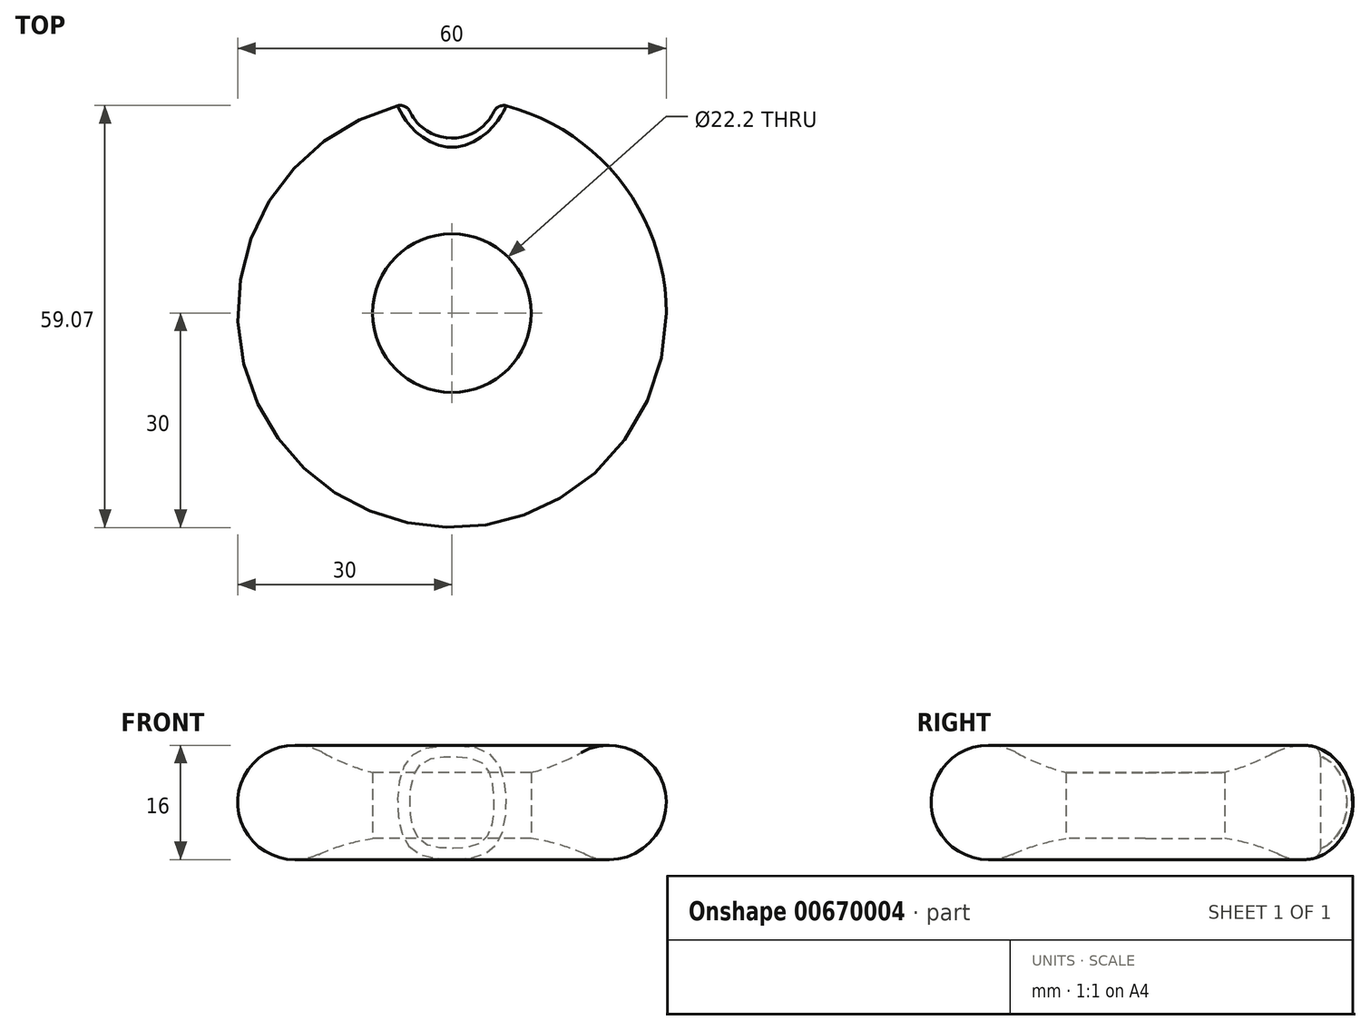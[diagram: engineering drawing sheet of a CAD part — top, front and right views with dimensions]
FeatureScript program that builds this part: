
annotation { "Feature Type Name" : "Feature", "Feature Type Description" : "" }
export const myFeature = defineFeature(function(context is Context, id is Id, definition is map)
    precondition{}
    {
        {
            var Q0;
            Q0=qCreatedBy(makeId("Right.planeOp"),FACE);
            var sketch = newSketch(context, id + "F0", { "sketchPlane" : qUnion([Q0])});
            skArc(sketch, "E0", {"start": v(-18.1, 14.99) * mm, "mid": v(-30, 8.33) * mm, "end": v(-18.7, 0.72) * mm});
            skPoint(sketch, "E1", {"position": v(-17.06, 7.86) * mm});
            skArc(sketch, "E2", {"start": v(0, 2.59) * mm, "mid": v(-9.5, 3.19) * mm, "end": v(-18.7, 0.72) * mm});
            skArc(sketch, "E3", {"start": v(-18.1, 14.99) * mm, "mid": v(-9.33, 11.8) * mm, "end": v(0, 11.53) * mm});
            skPoint(sketch, "E4.orphan", {"position": v(-16.89, 14.15) * mm});
            skPoint(sketch, "E5.orphan", {"position": v(-17.24, 1.57) * mm});
            skLineSegment(sketch, "E6", {"start": v(0, 11.53) * mm, "end": v(0, 2.59) * mm});
            skPoint(sketch, "E7.orphan", {"position": v(0, 13.3) * mm});
            skLineSegment(sketch, "E8.bottom", {"start": v(-3.38, 11.28) * mm, "end": v(1.79, 11.28) * mm});
            skLineSegment(sketch, "E8.top", {"start": v(-3.38, 13.04) * mm, "end": v(1.79, 13.04) * mm});
            skLineSegment(sketch, "E8.left", {"start": v(-3.38, 11.28) * mm, "end": v(-3.38, 13.04) * mm});
            skLineSegment(sketch, "E8.right", {"start": v(1.79, 11.28) * mm, "end": v(1.79, 13.04) * mm});
            skLineSegment(sketch, "E9.bottom", {"start": v(-5.05, 3.3) * mm, "end": v(5.31, 3.3) * mm});
            skLineSegment(sketch, "E9.top", {"start": v(-5.05, 0.65) * mm, "end": v(5.31, 0.65) * mm});
            skLineSegment(sketch, "E9.left", {"start": v(-5.05, 3.3) * mm, "end": v(-5.05, 0.65) * mm});
            skLineSegment(sketch, "E9.right", {"start": v(5.31, 3.3) * mm, "end": v(5.31, 0.65) * mm});
            skLineSegment(sketch, "E10.bottom", {"start": v(-5.05, 11.3) * mm, "end": v(3.19, 11.3) * mm});
            skLineSegment(sketch, "E10.top", {"start": v(-5.05, 12.11) * mm, "end": v(3.19, 12.11) * mm});
            skLineSegment(sketch, "E10.left", {"start": v(-5.05, 11.3) * mm, "end": v(-5.05, 12.11) * mm});
            skLineSegment(sketch, "E10.right", {"start": v(3.19, 11.3) * mm, "end": v(3.19, 12.11) * mm});
            skSolve(sketch);
        }
        {
            var Q0;
            {var subQ4=sQuery(id+"F0.wireOp",EDGE,"E0");Q0=makeQuery(id+"F0.imprint","IMPRINT",FACE,{"disambiguationData":[TD([[makeQuery(id+"F0.imprint","IMPRINT",EDGE,{"derivedFrom":subQ4}),1.0]])]});}
            var Q1;
            Q1=sQuery(id+"F0.wireOp",EDGE,"E6");
            revolve(context, id + "F1", {"entities" : qUnion([Q0]), "axis" : qUnion([Q1]), "revolveType" : RevolveType.FULL});
        }
        {
            var Q0;
            Q0=qCreatedBy(makeId("Top.planeOp"),FACE);
            var sketch = newSketch(context, id + "F2", { "sketchPlane" : qUnion([Q0])});
            skCircle(sketch, "E11", {"center": v(0, 0) * mm, "radius": 11.1 * mm});
            skSolve(sketch);
        }
        {
            var Q0;
            Q0 = qSketchRegion(id + "F2", true);
            extrude(context, id + "F3", {"entities" : qUnion([Q0]), "operationType" : NewBodyOperationType.REMOVE, "depth" : 25 * mm, "offsetDistance" : 25 * mm});
        }
        {
            var Q0;
            Q0=qCreatedBy(makeId("Top.planeOp"),FACE);
            var sketch = newSketch(context, id + "F4", { "sketchPlane" : qUnion([Q0])});
            skCircle(sketch, "E12", {"center": v(0, 31) * mm, "radius": 6.5 * mm});
            skSolve(sketch);
        }
        {
            var Q0;
            Q0 = qSketchRegion(id + "F4", true);
            extrude(context, id + "F5", {"entities" : qUnion([Q0]), "operationType" : NewBodyOperationType.REMOVE, "depth" : 25 * mm, "offsetDistance" : 25 * mm});
        }
        {
            var Q0;
            Q0=makeQuery(id+"F5.boolean.opBoolean","INTERSECT",EDGE,{"derivedFrom":[makeQuery(id+"F1.opRevolve","SWEPT_FACE",FACE,{"disambiguationData":[OSD([sQuery(id+"F0.wireOp",EDGE,"E0")])]}),makeQuery(id+"F5.opExtrude","SWEPT_FACE",FACE,{"disambiguationData":[OSD([sQuery(id+"F4.wireOp",EDGE,"E12")])]})]});
            fillet(context, id + "F6", {"entities" : qUnion([Q0]), "radius" : 1.5 * mm, "tangentPropagation" : true, "allowEdgeOverflow" : false});
        }
    });
